# Revit family: 0047510+3036809 Sylvania Lighting Fixture START FLAT PANEL LED UGR19 600 WW with SURFACE MOUNT FRAME
name_source: partatom
category: Lighting Fixtures
revit_build: Autodesk Revit 2017 (Build: 20190507_1515(x64)
units: mm (PartAtom-declared; Revit-internal decimal feet)

## family parameters
Cut with Voids When Loaded = No
Host = Face
Light Source = Yes
OmniClass Number = 23.80.70.11.17
OmniClass Title = Specialized Lighting by Location or Use
Part Type = Normal
Room Calculation Point = No
Round Connector Dimension = Use Diameter
Shared = No

## types (1)
- 0047510+3036809 START FLAT PANEL LED UGR19 600 WW with SURFACE MOUNT FRAME
    Apparent Load = 40 VA
    Assembly Code = D5020200
    AssetType = Fixed
    Color Filter = 16777215
    Default Elevation = 0 mm  [stored 0 ft]
    Description = Ultra thin LED Panel, excellent uniformity of light, perfect for ceilings with low voids, high efficacy.Ulta thin edgelit LED 600x600mm Panel with, excellent uniform light distribution. Acrylic PMMA diffuser optimising light output whilst reducing glare. 4239lm 93lm/W.
    Dimming Lamp Color Temperature Shift = <None>
    DocumentationLiterature = http://www.sylvania-lighting.com
    DurationUnit = hours
    ElectricShockClassification = Class II
    Emit Shape Visible in Rendering = No
    Emit from Rectangle Length = 545 mm  [stored 1.78806 ft]
    Emit from Rectangle Width = 545 mm  [stored 1.78806 ft]
    ExpectedLife = 50000
    HeightSMFrame_SYL = 54 mm  [stored 0.177165 ft]
    IfcExportAs = IfcLightFixtureType
    IfcExportType = IfcLightFixtureType
    ImpactProtectionIndex = IK05
    IngressProtection = IP20
    InputVoltage = 220-240V~
    Keynote = 16500
    Lamp = Integrated LED
    LampColourRenderingIndex = 80
    LampColourTemperature = 3000 K
    LampNominalLuminous = 3500 lm
    LampsType = Integrated LED
    LightOutputRatio = 100
    LuminousEfficacy = 88 lm/W
    Manufacturer = Feilo Sylvania
    ManufacturerName = Feilo Sylvania
    Material = powder coated steel housing, acrylic pmma diffuser
    Material_1_SYL = Polycarbonate_Sylvania_Startflat Panel LED_Opal
    Material_2_SYL = Metal_Sylvania_Startflat Panel LED_White
    Material_3_SYL = Metal_Sylvania_Startflat Panel LED_Silver
    Material_4_SYL = <By Category>
    Model = START FLAT PANEL LED UGR19 600 WW with SURFACE MOUNT FRAME
    ModelNumber = 0047510+3036809
    ModelReference = START FLAT PANEL LED UGR19 600 WW with SURFACE MOUNT FRAME
    Name = START FLAT PANEL LED UGR19 600 WW with SURFACE MOUNT FRAME
    NominalDepth = 602 mm  [stored 1.97507 ft]
    NominalHeight = 54 mm  [stored 0.177165 ft]
    NominalLength = 602 mm  [stored 1.97507 ft]
    Photometric Web File = 0047510.ies
    PowerConsumption = 40 W
    PowerFactor = 0
    Tilt Angle = -90.00°
    TypeName = START FLAT PANEL LED UGR19 600 WW with SURFACE MOUNT FRAME
    URL = http://www.sylvania-lighting.com
    Voltage = 230 V
    Weight = 18.5 kg

note: [stored X ft] marks values corroborated as IEEE doubles in the binary element streams (Revit-internal decimal feet)

## geometry (parser evidence)
native form markers: Sweep x2
no freeform markers — native parametric forms only
